# Revit family: Boitiers pour montages prises CEI
name_source: partatom
category: Installations électriques
revit_build: Autodesk Revit 2018 (Build: 20170223_1515(x64)
units: mm (PartAtom-declared; Revit-internal decimal feet)

## family parameters
Conserver l'orientation des annotations = Non
Cote de connecteur circulaire = Utiliser le diamètre
Couper avec des vides une fois chargée = Non
Hôte = Face
Partagée = Oui
Point de calcul de pièce = Non
Type d'élément = Normal

## types (1)
- Prise de montage 16A ou 32A avec sortie inclinée
    Description = Boitier pour le montage de prises au standard international saillie
    Diamètre entrée de câble = PG16/PG21
    Elévation par défaut = 1000 mm  [stored 3.28084 ft]
    Fabricant = Legrand
    Famille produit = 0852-P17
    IDS_MONTAGE_PRISE_VERROUILLEE = Non
    Intensité A = 16 A
    Modèle = LG-057750
    Température maximum d'utilisation = 40°C
    Température minimum d'utilisation = -25°C
    entraxe de fixation horizontal mm = 75 mm
    entraxe de fixation vertical mm = 85 mm
    hauteur mm = 97 mm
    largeur mm = 87 mm
    matériau du boitier = plastique
    profondeur mm = 97 mm
    résistance aux chocs IK = 08
    sans halogène = Oui

note: [stored X ft] marks values corroborated as IEEE doubles in the binary element streams (Revit-internal decimal feet)
